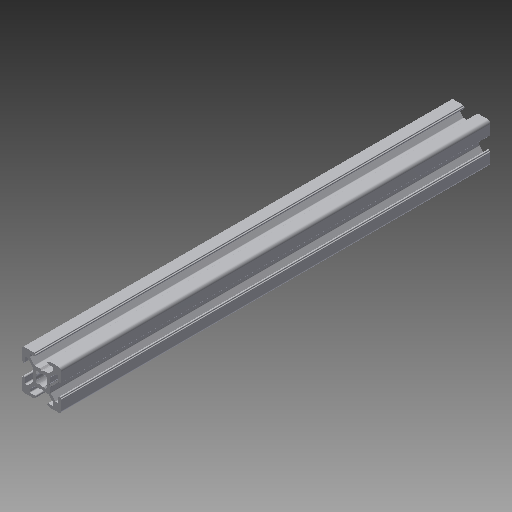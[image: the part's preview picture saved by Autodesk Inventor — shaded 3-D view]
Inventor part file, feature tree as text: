
AUTODESK INVENTOR PART (.ipt)
format: ipt  version: 2019 (Build 230136000, 136)  size: 307,712 bytes
history: native  units: in
note: dims shown in document units (in); Inventor stores cm internally (conversion verified against a paired STEP export)
features: other x3, extrude x1, sketch x1
ambient origin geometry x8: Origin, YZ Plane, XZ Plane, XY Plane, X Axis, Y Axis, Z Axis, Center Point
bodies: Solid1 (feature_tree)
feature tree (5):
  other  "Blocks"
  extrude  "Extrusion1"  Depth=1.0in
  sketch  "Sketch1"  dims[d1=0.0in d13=1.0in d14=1.0in]
  other  "20x20"
  other  "20x20:1"
